# Revit family: UM 1000
name_source: partatom
category: Осветительные приборы
revit_build: Autodesk Revit 2016 (Build: 20161004_0715(x64)
units: mm (PartAtom-declared; Revit-internal decimal feet)

## family parameters
Источник света = Нет
Общий = Нет
Основа = Грань
При загрузке вырезать с полостями = Нет
Размер круглого соединителя = Использовать диаметр
Тип детали = Нормальный
Точка расчета площади = Нет

## types (1)
- UM 1000
    ADSK_Классификация нагрузок = Прочее
    ADSK_Код изделия = 1355000010
    ADSK_Количество фаз = 1
    ADSK_Количество фаз числовое = 1
    ADSK_Коэффициент мощности = 0.85
    ADSK_Масса = 25.4
    ADSK_Напряжение = 230 В
    ADSK_Номинальная мощность = 1 кВт
    ADSK_Полная мощность = 1 кВ·А
    ADSK_Размер_Высота = 695 мм
    ADSK_Размер_Длина = 469 мм
    ADSK_Размер_Радиус = 15 мм
    ADSK_Размер_Толщина = 233 мм
    ADSK_Размер_Ширина = 407 мм
    ADSK_Ток = 5 А
    ADSK_Энергоэффективность = 0 лм/Вт
    IP Class = IP66
    L = 160 мм
    URL = https://www.ltcompany.com
    Блок аварийного питания = Нет
    Блок.высота = 140 мм
    Блок.длина = 328 мм
    Блок.толщина = 163 мм
    Выбор ИС = IES_UM 1000 : UMS 1000H 5000K 90000
    Группа модели = Светильники
    Да = Нет
    Изготовитель = ООО МГК Световые технологии
    Класс Защиты = I
    Класс пожароопасности = П-ІІІ
    Климатическая зона = УХЛ1
    Код по классификатору = D5020200
    Корпус = Cерый металл
    Нет = Нет
    Область использования = Освещение дорог, Открытые спортивные площадки, Промышленные предприятия, Складские объекты, Стадионы
    Описание = Прожекторы серии UM обладают широким выбором оптических систем для любого применения. Простая установка и обслуживание, отдельный блок ПРА и высокий КПД оптической системы дают возможность применения данных прожекторов как для спортивного, так и для функционального и промышленного освещения
    Отметка по умолчанию = 0 мм
    Отражатель = Корпус металл
    Плафон = Плафон прозрачный
    Полная установленная мощность = 1 кВ·А
    Тип ИС = МГЛ
    Тип продукции = Светильник

## geometry (parser evidence)
native form markers: Blend x4
no freeform markers — native parametric forms only
